# Revit family: Shower-Showerhead-KOHLER-Purist-K-22170BR_1
name_source: partatom
category: Plumbing Fixtures
units: mm (PartAtom-declared; Revit-internal decimal feet)

## family parameters
Cut with Voids When Loaded = No
Host = Face
OmniClass Number = 23.31.17.00
OmniClass Title = Showers
Part Type = Normal
Room Calculation Point = No
Round Connector Dimension = Use Diameter
Shared = No

## types (4) — shared parameters
ADA Compliant = No
Assembly Code = D2010700
CW Connection = No
Cold Water Inlet = Cold Water Inlet
Date Modified = 09/22/2022
Default Elevation = 42"
Description = Multi-Function Showerhead 2.5GPM
Drain Included = No
Flow Rate = 3 GPM
HW Connection = Yes
Height = 4 1/16"
Hot Water Inlet = Tempered Water Inlet
Length = 5 1/2"
Manufacturer = Kohler Co.
Master Format 2014 = 22 42 23
Master Format 2014 Name = Residential Showers
Material = Plastic
Pressure = 45.00 psi
Product Name = Purist
URL = https://br.kohler.com
Vent Connection = No
Waste Connection = No
Waste Water Outlet = Waste Water Outlet
WaterSense Certified = No
Width = 5 1/2"

## per-type parameters (varying)
| type | Finish | Model | Product Page URL | Type |
| BL-Matte Black | Kohler-Plastic-BL-Matte_Black | K-22170BR-BL |  | 1 |
| BN-Vibrant Brushed Nickel | KOHLER-Plastic-BN-Vibrant_Brushed_Nickel | K-22170BR-BN | https://br.kohler.com | 2 |
| RGD-Polished Rose Gold | Kohler-Plastic-RGD-Polished_Rose_Gold | K-22170BR-RGD | https://br.kohler.com | 4 |
| CP-Polished Chrome | Kohler-Plastic-CP-Polished_Chrome | K-22170BR-CP | https://br.kohler.com | 3 |

## geometry (parser evidence)
native form markers: Sweep x5
no freeform markers — native parametric forms only
